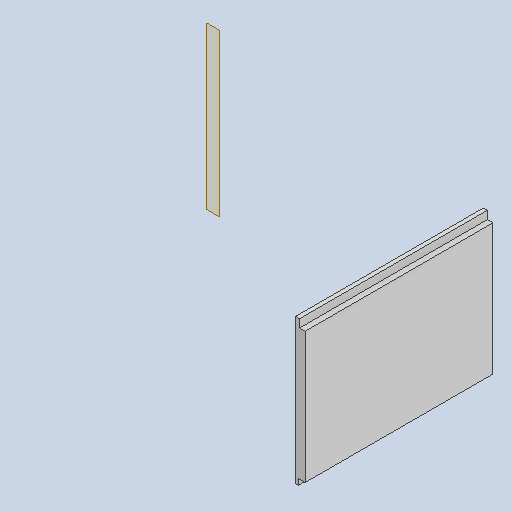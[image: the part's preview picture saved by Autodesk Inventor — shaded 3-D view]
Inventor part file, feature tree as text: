
AUTODESK INVENTOR PART (.ipt)
format: ipt  version: 2022 (Build 260153000, 153)  size: 98,816 bytes
history: native  units: in
note: dims shown in document units (in); Inventor stores cm internally (conversion verified against a paired STEP export)
features: other x3, plane x1, extrude x1, sketch x1, reference x1
ambient origin geometry x8: Origin, YZ Plane, XZ Plane, XY Plane, X Axis, Y Axis, Z Axis, Center Point
bodies: Solid1 (feature_tree)
feature tree (7):
  plane  "Work Plane1"
  extrude  "Extrusion1"  Depth=4.8in TaperAngle=0.0deg
  sketch  "Sketch1"  dims[d0=0.0275in d1=4.8in d2=0.0in]
  reference  "Reference1"
  other  "<userpath>\OneDrive\Desktop\Smarty Plants Files\Assembly1.iam"
  other  "Assembly1.iam"
  other  "SqPot:1"
